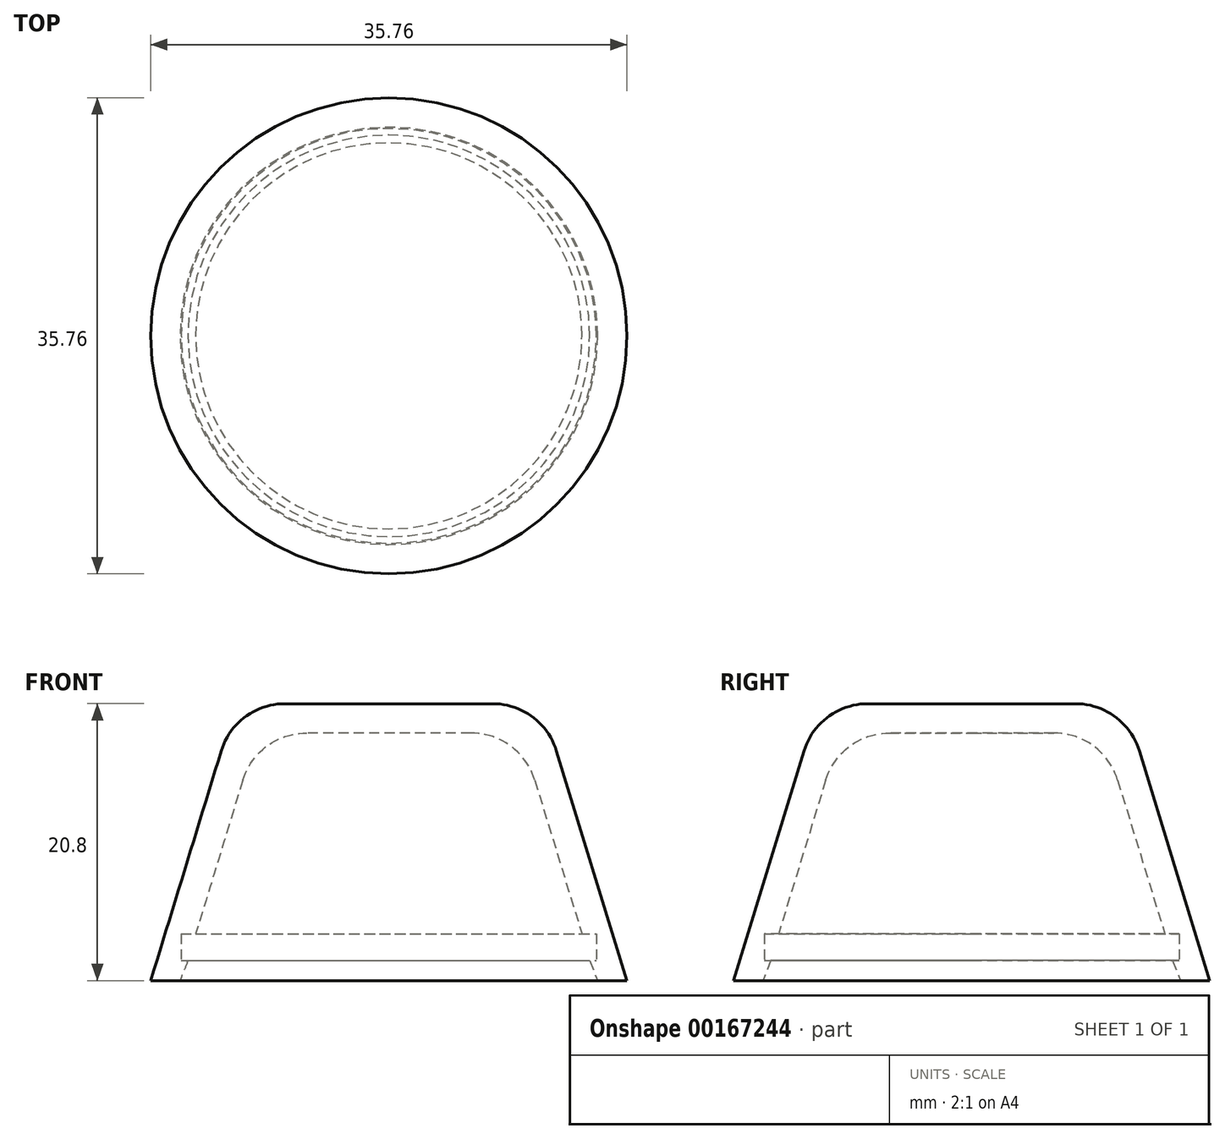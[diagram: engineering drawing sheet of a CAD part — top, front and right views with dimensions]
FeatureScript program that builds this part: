
annotation { "Feature Type Name" : "Feature", "Feature Type Description" : "" }
export const myFeature = defineFeature(function(context is Context, id is Id, definition is map)
    precondition{}
    {
        {
            var Q0;
            Q0=qCreatedBy(makeId("Front.planeOp"),FACE);
            var sketch = newSketch(context, id + "F0", { "sketchPlane" : qUnion([Q0])});
            skLineSegment(sketch, "E0", {"start": v(17.88, -8.61) * mm, "end": v(11.5, 12.19) * mm});
            skLineSegment(sketch, "E1", {"start": v(11.5, 12.19) * mm, "end": v(0, 12.19) * mm});
            skLineSegment(sketch, "E2.0", {"start": v(9.87, 9.99) * mm, "end": v(0, 9.99) * mm});
            skLineSegment(sketch, "E2.1", {"start": v(14.5, -5.11) * mm, "end": v(9.87, 9.99) * mm});
            skLineSegment(sketch, "E3", {"start": v(17.88, -8.61) * mm, "end": v(15.68, -8.61) * mm});
            skLineSegment(sketch, "E4", {"start": v(15.68, -8.61) * mm, "end": v(15.08, -7.11) * mm});
            skLineSegment(sketch, "E5", {"start": v(15.08, -7.11) * mm, "end": v(15.58, -7.11) * mm});
            skLineSegment(sketch, "E6", {"start": v(15.58, -7.11) * mm, "end": v(15.58, -5.11) * mm});
            skLineSegment(sketch, "E7", {"start": v(15.58, -5.11) * mm, "end": v(14.5, -5.11) * mm});
            skLineSegment(sketch, "E8", {"start": v(0, 12.19) * mm, "end": v(0, 9.99) * mm});
            skLineSegment(sketch, "E9", {"start": v(0, 0) * mm, "end": v(0, 17.55) * mm, "construction": true});
            skSolve(sketch);
        }
        {
            var Q0;
            Q0 = qSketchRegion(id + "F0", true);
            var Q1;
            Q1=sQuery(id+"F0.wireOp",EDGE,"E9");
            revolve(context, id + "F1", {"entities" : qUnion([Q0]), "axis" : qUnion([Q1]), "revolveType" : RevolveType.FULL});
        }
        {
            var Q0;
            Q0=makeQuery(id+"F1.opRevolve","SWEPT_EDGE",EDGE,{"disambiguationData":[OSD([sQuery(id+"F0.wireOp",EDGE,"E0"),sQuery(id+"F0.wireOp",EDGE,"E1")])]});
            var Q1;
            Q1=makeQuery(id+"F1.opRevolve","SWEPT_EDGE",EDGE,{"disambiguationData":[OSD([sQuery(id+"F0.wireOp",EDGE,"E2.0"),sQuery(id+"F0.wireOp",EDGE,"E2.1")])]});
            fillet(context, id + "F2", {"entities" : qUnion([Q0, Q1]), "radius" : 5 * mm, "tangentPropagation" : true, "allowEdgeOverflow" : false});
        }
    });
